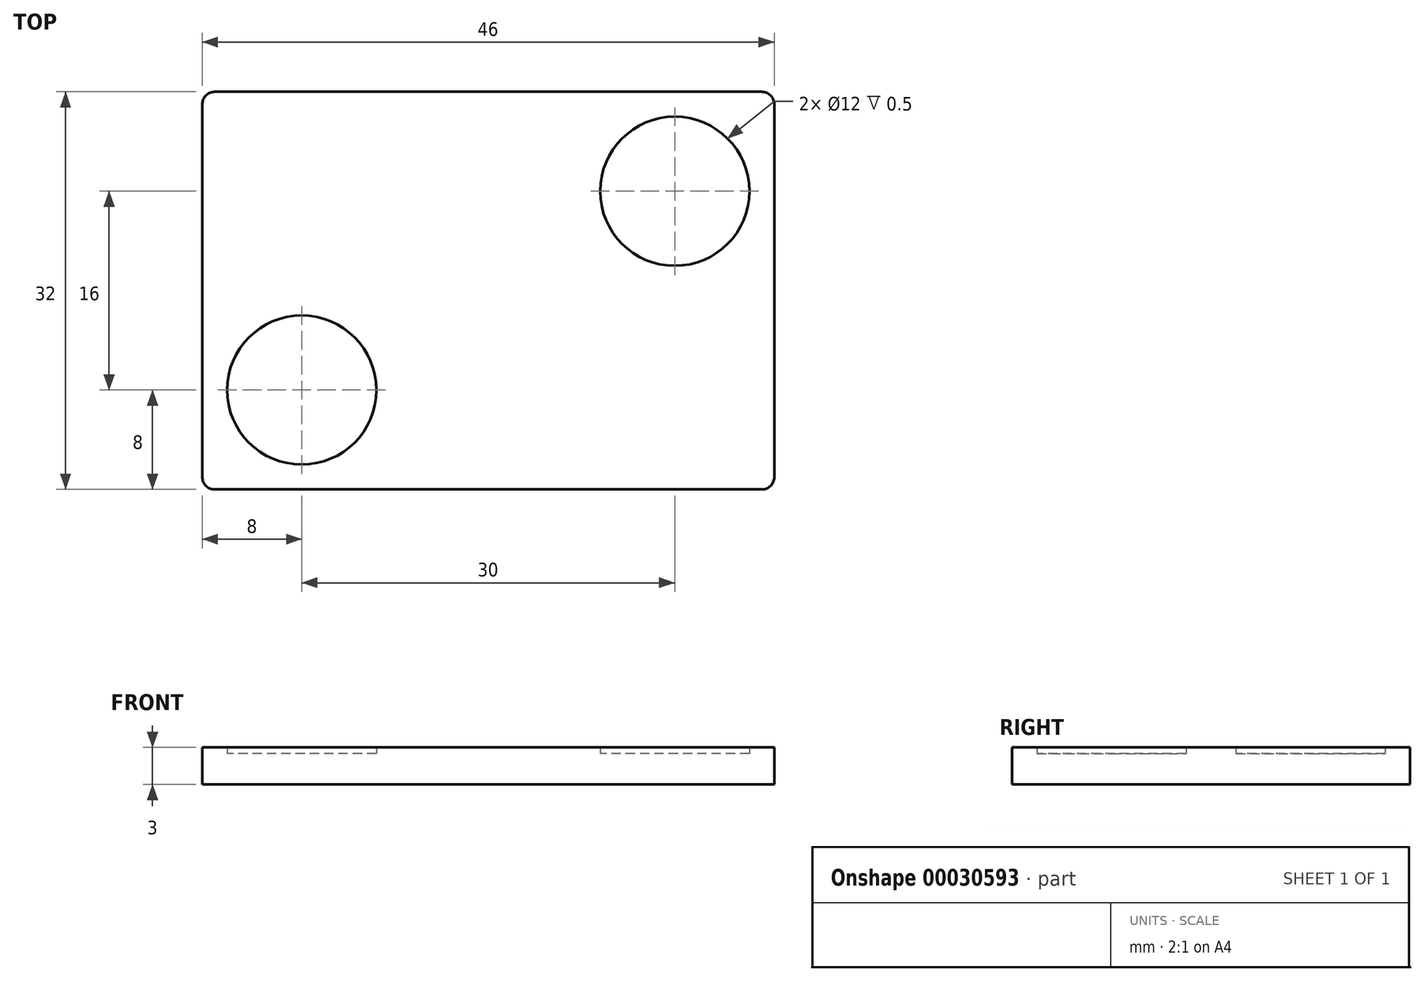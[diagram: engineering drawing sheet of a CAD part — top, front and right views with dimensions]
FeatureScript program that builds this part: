
annotation { "Feature Type Name" : "Feature", "Feature Type Description" : "" }
export const myFeature = defineFeature(function(context is Context, id is Id, definition is map)
    precondition{}
    {
        {
            var Q0;
            Q0=qCreatedBy(makeId("Top.planeOp"),FACE);
            var sketch = newSketch(context, id + "F0", { "sketchPlane" : qUnion([Q0])});
            skLineSegment(sketch, "E0.rect.bottom", {"start": v(-23, 16) * mm, "end": v(23, 16) * mm});
            skLineSegment(sketch, "E0.rect.top", {"start": v(-23, -16) * mm, "end": v(23, -16) * mm});
            skLineSegment(sketch, "E0.rect.left", {"start": v(-23, 16) * mm, "end": v(-23, -16) * mm});
            skLineSegment(sketch, "E0.rect.right", {"start": v(23, 16) * mm, "end": v(23, -16) * mm});
            skPoint(sketch, "E0.rect.middle", {"position": v(0, 0) * mm});
            skSolve(sketch);
        }
        {
            var Q0;
            Q0=makeQuery(id+"F0.imprint","IMPRINT",FACE,{"disambiguationData":[TD([[makeQuery(id+"F0.imprint","IMPRINT",EDGE,{"derivedFrom":sQuery(id+"F0.wireOp",EDGE,"E0.rect.bottom")}),-1.0]])]});
            extrude(context, id + "F1", {"entities" : qUnion([Q0]), "depth" : 2.5 * mm});
        }
        {
            var Q0;
            Q0=makeQuery(id+"F1.opExtrude","CAP_FACE",FACE,{"disambiguationData":[OSD([sQuery(id+"F0.wireOp",EDGE,"E0.rect.bottom"),sQuery(id+"F0.wireOp",EDGE,"E0.rect.top"),sQuery(id+"F0.wireOp",EDGE,"E0.rect.left"),sQuery(id+"F0.wireOp",EDGE,"E0.rect.right")])],"isStart":false});
            var sketch = newSketch(context, id + "F2", { "sketchPlane" : qUnion([Q0])});
            skCircle(sketch, "E1", {"center": v(-15, 8) * mm, "radius": 6 * mm});
            skCircle(sketch, "E2.MirrorC", {"center": v(-15, -8) * mm, "radius": 6 * mm});
            skCircle(sketch, "E3.MirrorC", {"center": v(15, 8) * mm, "radius": 6 * mm});
            skCircle(sketch, "E4.MirrorC", {"center": v(15, -8) * mm, "radius": 6 * mm});
            skSolve(sketch);
        }
        {
            var Q0;
            Q0=makeQuery(id+"F2.imprint","IMPRINT",FACE,{"disambiguationData":[TD([[makeQuery(id+"F2.imprint","IMPRINT",EDGE,{"derivedFrom":sQuery(id+"F2.wireOp",EDGE,"E1")}),1.0]])]});
            var Q1;
            Q1=makeQuery(id+"F2.imprint","IMPRINT",FACE,{"disambiguationData":[TD([[makeQuery(id+"F2.imprint","IMPRINT",EDGE,{"derivedFrom":sQuery(id+"F2.wireOp",EDGE,"E3.MirrorC")}),-1.0]])]});
            var Q2;
            Q2=makeQuery(id+"F2.imprint","IMPRINT",FACE,{"disambiguationData":[TD([[makeQuery(id+"F2.imprint","IMPRINT",EDGE,{"derivedFrom":sQuery(id+"F2.wireOp",EDGE,"E2.MirrorC")}),-1.0]])]});
            var Q3;
            Q3=makeQuery(id+"F2.imprint","IMPRINT",FACE,{"disambiguationData":[TD([[makeQuery(id+"F2.imprint","IMPRINT",EDGE,{"derivedFrom":sQuery(id+"F2.wireOp",EDGE,"E4.MirrorC")}),1.0]])]});
            extrude(context, id + "F3", {"entities" : qUnion([Q0, Q1, Q2, Q3]), "operationType" : NewBodyOperationType.ADD, "depth" : 0.5 * mm});
        }
        {
            var Q0;
            Q0=makeQuery(id+"F1.opExtrude","SWEPT_EDGE",EDGE,{"disambiguationData":[OSD([sQuery(id+"F0.wireOp",EDGE,"E0.rect.top"),sQuery(id+"F0.wireOp",EDGE,"E0.rect.right")])]});
            var Q1;
            Q1=makeQuery(id+"F1.opExtrude","SWEPT_EDGE",EDGE,{"disambiguationData":[OSD([sQuery(id+"F0.wireOp",EDGE,"E0.rect.top"),sQuery(id+"F0.wireOp",EDGE,"E0.rect.left")])]});
            var Q2;
            Q2=makeQuery(id+"F1.opExtrude","SWEPT_EDGE",EDGE,{"disambiguationData":[OSD([sQuery(id+"F0.wireOp",EDGE,"E0.rect.bottom"),sQuery(id+"F0.wireOp",EDGE,"E0.rect.right")])]});
            var Q3;
            Q3=makeQuery(id+"F1.opExtrude","SWEPT_EDGE",EDGE,{"disambiguationData":[OSD([sQuery(id+"F0.wireOp",EDGE,"E0.rect.bottom"),sQuery(id+"F0.wireOp",EDGE,"E0.rect.left")])]});
            fillet(context, id + "F4", {"entities" : qUnion([Q0, Q1, Q2, Q3]), "radius" : 1 * mm, "tangentPropagation" : true, "allowEdgeOverflow" : false});
        }
    });
